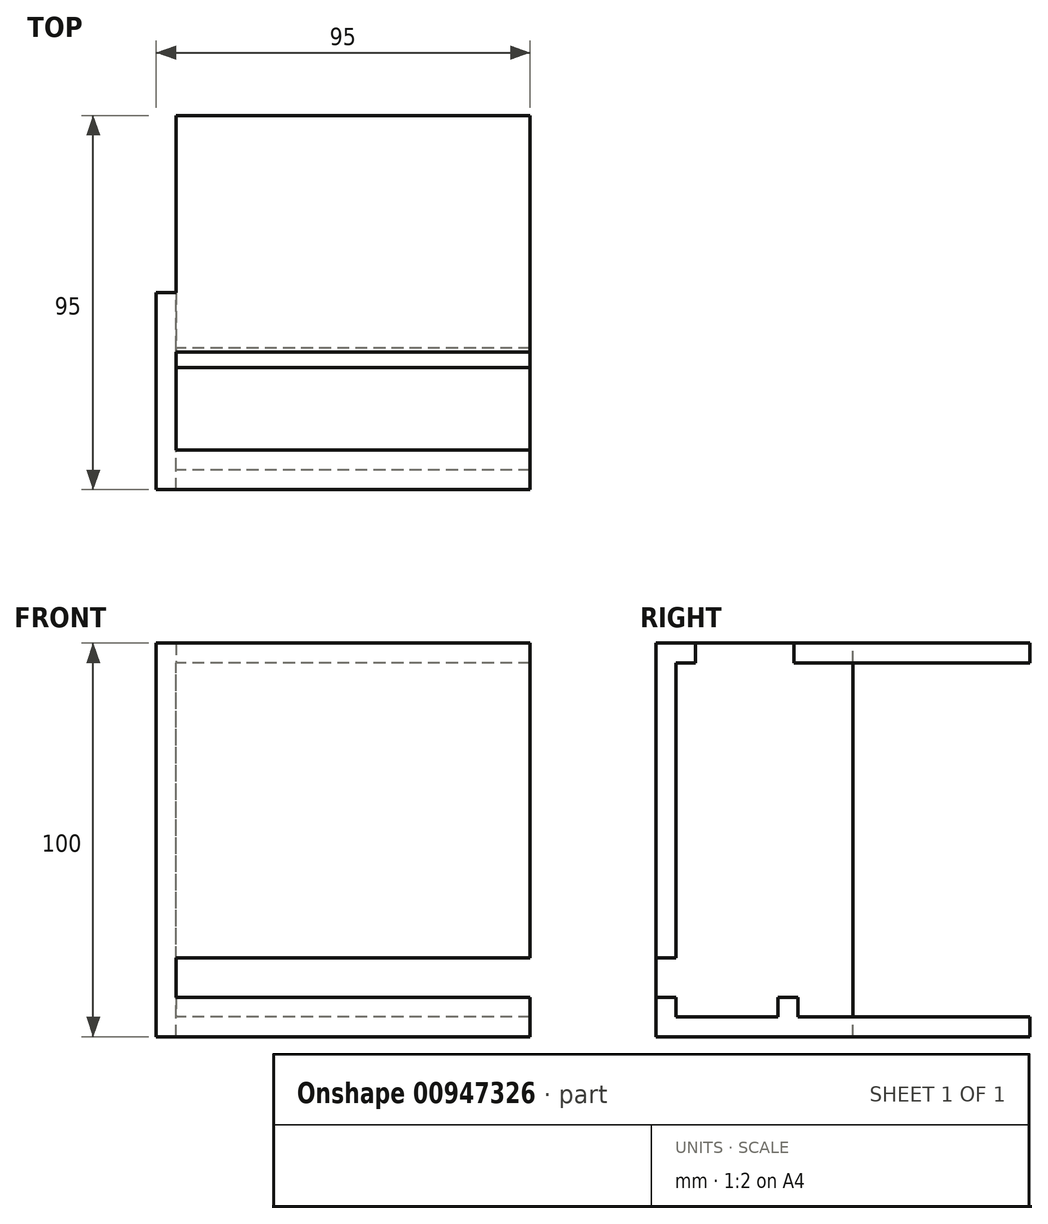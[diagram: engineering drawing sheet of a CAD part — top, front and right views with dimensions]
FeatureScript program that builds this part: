
annotation { "Feature Type Name" : "Feature", "Feature Type Description" : "" }
export const myFeature = defineFeature(function(context is Context, id is Id, definition is map)
    precondition{}
    {
        {
            var Q0;
            Q0=qCreatedBy(makeId("Top.planeOp"),FACE);
            var sketch = newSketch(context, id + "F0", { "sketchPlane" : qUnion([Q0])});
            skLineSegment(sketch, "E0", {"start": v(0, 0) * mm, "end": v(0, 10) * mm});
            skLineSegment(sketch, "E1", {"start": v(0, 10) * mm, "end": v(5, 10) * mm});
            skLineSegment(sketch, "E2", {"start": v(5, 10) * mm, "end": v(5, 5) * mm});
            skLineSegment(sketch, "E3", {"start": v(5, 5) * mm, "end": v(95, 5) * mm});
            skLineSegment(sketch, "E4", {"start": v(95, 5) * mm, "end": v(95, 0) * mm});
            skLineSegment(sketch, "E5", {"start": v(95, 0) * mm, "end": v(0, 0) * mm});
            skLineSegment(sketch, "E6.bottom", {"start": v(31, 5) * mm, "end": v(36, 5) * mm});
            skLineSegment(sketch, "E6.top", {"start": v(31, 10) * mm, "end": v(36, 10) * mm});
            skLineSegment(sketch, "E6.left", {"start": v(31, 5) * mm, "end": v(31, 10) * mm});
            skLineSegment(sketch, "E6.right", {"start": v(36, 5) * mm, "end": v(36, 10) * mm});
            skSolve(sketch);
        }
        {
            var Q0;
            Q0=qCreatedBy(makeId("Top.planeOp"),FACE);
            var sketch = newSketch(context, id + "F1", { "sketchPlane" : qUnion([Q0])});
            skLineSegment(sketch, "E7", {"start": v(0, 20) * mm, "end": v(5, 20) * mm});
            skLineSegment(sketch, "E8", {"start": v(5, 20) * mm, "end": v(5, 95) * mm});
            skLineSegment(sketch, "E9", {"start": v(5, 95) * mm, "end": v(10, 95) * mm});
            skLineSegment(sketch, "E10", {"start": v(10, 95) * mm, "end": v(10, 100) * mm});
            skLineSegment(sketch, "E11", {"start": v(10, 100) * mm, "end": v(0, 100) * mm});
            skLineSegment(sketch, "E12", {"start": v(0, 100) * mm, "end": v(0, 20) * mm});
            skSolve(sketch);
        }
        {
            var Q0;
            Q0=qCreatedBy(makeId("Top.planeOp"),FACE);
            var sketch = newSketch(context, id + "F2", { "sketchPlane" : qUnion([Q0])});
            skLineSegment(sketch, "E13.bottom", {"start": v(95, 100) * mm, "end": v(35, 100) * mm});
            skLineSegment(sketch, "E13.top", {"start": v(95, 95) * mm, "end": v(35, 95) * mm});
            skLineSegment(sketch, "E13.left", {"start": v(95, 100) * mm, "end": v(95, 95) * mm});
            skLineSegment(sketch, "E13.right", {"start": v(35, 100) * mm, "end": v(35, 95) * mm});
            skSolve(sketch);
        }
        {
            var Q0;
            Q0=qCreatedBy(makeId("Top.planeOp"),FACE);
            var sketch = newSketch(context, id + "F3", { "sketchPlane" : qUnion([Q0])});
            skLineSegment(sketch, "E14.bottom", {"start": v(0, 0) * mm, "end": v(50, 0) * mm});
            skLineSegment(sketch, "E14.top", {"start": v(0, 100) * mm, "end": v(50, 100) * mm});
            skLineSegment(sketch, "E14.left", {"start": v(0, 0) * mm, "end": v(0, 100) * mm});
            skLineSegment(sketch, "E14.right", {"start": v(50, 0) * mm, "end": v(50, 100) * mm});
            skSolve(sketch);
        }
        {
            var Q0;
            Q0=makeQuery(id+"F3.imprint","IMPRINT",FACE,{"disambiguationData":[TD([[makeQuery(id+"F3.imprint","IMPRINT",EDGE,{"derivedFrom":sQuery(id+"F3.wireOp",EDGE,"E14.bottom")}),1.0]])]});
            extrude(context, id + "F4", {"entities" : qUnion([Q0]), "oppositeDirection" : true, "depth" : 5 * mm, "offsetDistance" : 25 * mm});
        }
        {
            var Q0;
            Q0 = qSketchRegion(id + "F0", true);
            var Q1;
            Q1 = qSketchRegion(id + "F1", true);
            var Q2;
            Q2 = qSketchRegion(id + "F2", true);
            extrude(context, id + "F5", {"entities" : qUnion([Q0, Q1, Q2]), "operationType" : NewBodyOperationType.ADD, "surfaceOperationType" : NewSurfaceOperationType.ADD, "depth" : 90 * mm, "offsetDistance" : 25 * mm});
        }
        {
            var Q0;
            Q0=makeQuery(id+"F4.opExtrude","SWEPT_BODY",BODY,{"disambiguationData":[OSD([sQuery(id+"F3.wireOp",EDGE,"E14.bottom"),sQuery(id+"F3.wireOp",EDGE,"E14.top"),sQuery(id+"F3.wireOp",EDGE,"E14.left"),sQuery(id+"F3.wireOp",EDGE,"E14.right")])]});
            var Q1;
            Q1=makeQuery(id+"F4.opExtrude","CAP_EDGE",EDGE,{"disambiguationData":[OSD([sQuery(id+"F3.wireOp",EDGE,"E14.bottom")])],"isStart":false});
            transform(context, id + "F6", {"entities" : qUnion([Q0]), "transformType" : TransformType.ROTATION, "transformAxis" : qUnion([Q1]), "angle" : 90 * degree, "makeCopy" : false});
        }
        {
            var Q0;
            Q0=makeQuery(id+"F4.opExtrude","SWEPT_BODY",BODY,{"disambiguationData":[OSD([sQuery(id+"F3.wireOp",EDGE,"E14.bottom"),sQuery(id+"F3.wireOp",EDGE,"E14.top"),sQuery(id+"F3.wireOp",EDGE,"E14.left"),sQuery(id+"F3.wireOp",EDGE,"E14.right")])]});
            var Q1;
            Q1=makeQuery(id+"F4.opExtrude","CAP_EDGE",EDGE,{"disambiguationData":[OSD([sQuery(id+"F3.wireOp",EDGE,"E14.left")])],"isStart":false});
            var Q2;
            Q2=makeQuery(id+"F4.opExtrude","CAP_EDGE",EDGE,{"disambiguationData":[OSD([sQuery(id+"F3.wireOp",EDGE,"E14.left")])],"isStart":false});
            transform(context, id + "F7", {"entities" : qUnion([Q0]), "transformType" : TransformType.ROTATION, "transformAxis" : qUnion([Q2]), "angle" : 90 * degree, "makeCopy" : false});
        }
    });
